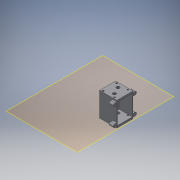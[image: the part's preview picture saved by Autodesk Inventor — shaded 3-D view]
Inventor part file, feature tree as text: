
AUTODESK INVENTOR PART (.ipt)
format: ipt  version: 2017 (Build 210142000, 142)  size: 279,552 bytes
history: native  units: mm
features: extrude x6, sketch x6, projected_geometry x6, other x3, plane x1, reference x1
ambient origin geometry x8: Origin, YZ Plane, XZ Plane, XY Plane, X Axis, Y Axis, Z Axis, Center Point
bodies: Solid1 (feature_tree)
feature tree (23):
  plane  "Work Plane1"
  extrude  "Extrusion1"  Depth=38.0mm
  extrude  "Extrusion2"  Depth=50.0mm TaperAngle=0.0deg
  extrude  "Extrusion3"  Depth=5.0mm TaperAngle=0.0deg
  extrude  "Extrusion4"  Depth=6.0mm
  extrude  "Extrusion5"  Depth=5.0mm TaperAngle=0.0deg
  extrude  "Extrusion6"  Depth=50.0mm
  sketch  "Sketch1"  dims[d0=3.81mm d1=38.0mm]
  reference  "Reference1"
  sketch  "Sketch2"  dims[d2=5.0mm d3=0.0mm d4=50.0mm d5=0.0mm]
  projected_geometry  "Projected Loop1"
  sketch  "Sketch3"  dims[d6=5.0mm d7=0.0mm d8=5.0mm d9=0.0mm]
  projected_geometry  "Projected Loop2"
  projected_geometry  "Projected Loop3"
  sketch  "Sketch4"  dims[d10=5.0mm d11=6.0mm]
  projected_geometry  "Projected Loop4"
  sketch  "Sketch5"  dims[d12=5.0mm d13=15.0mm d14=0.0mm]
  projected_geometry  "Projected Loop5"
  sketch  "Sketch6"  dims[d15=2.5mm d16=50.0mm d17=45.0mm d18=4.0mm d19=10.0mm d20=0.0mm]
  projected_geometry  "Projected Loop6"
  parser-record x1  (decoder bookkeeping rows leaked as tree rows — omitted from the tree; the rows remain in map.json)
  other  "gearbox.iam"
  other  "case part 1:1"
note: 1 file-system path scrubbed to <path> (originals preserved in map.json)
